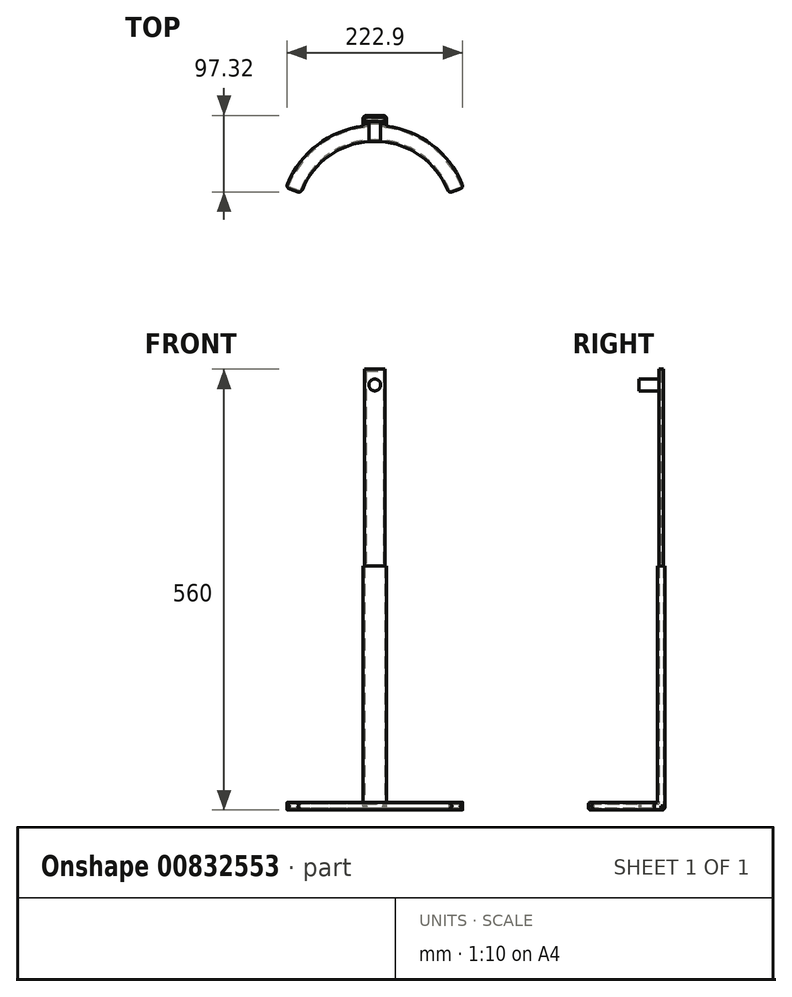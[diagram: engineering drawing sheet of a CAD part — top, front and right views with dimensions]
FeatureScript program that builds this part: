
annotation { "Feature Type Name" : "Feature", "Feature Type Description" : "" }
export const myFeature = defineFeature(function(context is Context, id is Id, definition is map)
    precondition{}
    {
        {
            var Q0;
            Q0=qCreatedBy(makeId("Right.planeOp"),FACE);
            var sketch = newSketch(context, id + "F0", { "sketchPlane" : qUnion([Q0])});
            skLineSegment(sketch, "E0.bottom", {"start": v(30, 5) * mm, "end": v(50, 5) * mm});
            skLineSegment(sketch, "E0.top", {"start": v(30, -5) * mm, "end": v(50, -5) * mm});
            skLineSegment(sketch, "E0.left", {"start": v(30, 5) * mm, "end": v(30, -5) * mm});
            skLineSegment(sketch, "E0.right", {"start": v(50, 5) * mm, "end": v(50, -5) * mm});
            skLineSegment(sketch, "E1", {"start": v(-70, 26.35) * mm, "end": v(-70, -22.57) * mm});
            skSolve(sketch);
        }
        {
            var Q0;
            Q0=makeQuery(id+"F0.imprint","IMPRINT",FACE,{"disambiguationData":[TD([[makeQuery(id+"F0.imprint","IMPRINT",EDGE,{"derivedFrom":sQuery(id+"F0.wireOp",EDGE,"E0.bottom")}),-1.0]])]});
            var Q1;
            Q1=sQuery(id+"F0.wireOp",EDGE,"E1");
            revolve(context, id + "F1", {"surfaceOperationType" : NewSurfaceOperationType.NEW, "entities" : qUnion([Q0]), "axis" : qUnion([Q1]), "revolveType" : RevolveType.SYMMETRIC, "angle" : 140 * degree});
        }
        {
            var Q0;
            Q0=qCreatedBy(makeId("Right.planeOp"),FACE);
            var sketch = newSketch(context, id + "F2", { "sketchPlane" : qUnion([Q0])});
            skLineSegment(sketch, "E2.bottom", {"start": v(41.95, 5) * mm, "end": v(62.75, 5) * mm});
            skLineSegment(sketch, "E2.top", {"start": v(41.95, -5) * mm, "end": v(62.75, -5) * mm});
            skLineSegment(sketch, "E2.left", {"start": v(41.95, 5) * mm, "end": v(41.95, -5) * mm});
            skLineSegment(sketch, "E2.right", {"start": v(62.75, 5) * mm, "end": v(62.75, -5) * mm});
            skSolve(sketch);
        }
        {
            var Q0;
            Q0=makeQuery(id+"F2.imprint","IMPRINT",FACE,{"disambiguationData":[TD([[makeQuery(id+"F2.imprint","IMPRINT",EDGE,{"derivedFrom":sQuery(id+"F2.wireOp",EDGE,"E2.bottom")}),-1.0]])]});
            extrude(context, id + "F3", {"entities" : qUnion([Q0]), "operationType" : NewBodyOperationType.ADD, "endBound" : BoundingType.SYMMETRIC, "depth" : 30 * mm, "offsetDistance" : 25 * mm});
        }
        {
            var Q0;
            Q0=makeQuery(id+"F3.boolean.opBoolean","MERGE",FACE,{"derivedFrom":[makeQuery(id+"F1.opRevolve","SWEPT_FACE",FACE,{"disambiguationData":[OSD([sQuery(id+"F0.wireOp",EDGE,"E0.bottom")])]}),makeQuery(id+"F3.opExtrude","SWEPT_FACE",FACE,{"disambiguationData":[OSD([sQuery(id+"F2.wireOp",EDGE,"E2.bottom")])]})]});
            var sketch = newSketch(context, id + "F4", { "sketchPlane" : qUnion([Q0])});
            skLineSegment(sketch, "E3.bottom", {"start": v(-15, 62.75) * mm, "end": v(15, 62.75) * mm});
            skLineSegment(sketch, "E3.top", {"start": v(-15, 52.75) * mm, "end": v(15, 52.75) * mm});
            skLineSegment(sketch, "E3.left", {"start": v(-15, 62.75) * mm, "end": v(-15, 52.75) * mm});
            skLineSegment(sketch, "E3.right", {"start": v(15, 62.75) * mm, "end": v(15, 52.75) * mm});
            skSolve(sketch);
        }
        {
            var Q0;
            Q0 = qSketchRegion(id + "F4", true);
            extrude(context, id + "F5", {"entities" : qUnion([Q0]), "operationType" : NewBodyOperationType.ADD, "depth" : 300 * mm, "offsetDistance" : 25 * mm});
        }
        {
            var Q0;
            Q0=makeQuery(id+"F5.opExtrude","CAP_FACE",FACE,{"disambiguationData":[OSD([sQuery(id+"F4.wireOp",EDGE,"E3.bottom"),sQuery(id+"F4.wireOp",EDGE,"E3.top"),sQuery(id+"F4.wireOp",EDGE,"E3.left"),sQuery(id+"F4.wireOp",EDGE,"E3.right")])],"isStart":false});
            shell(context, id + "F6", {"entities" : qUnion([Q0]), "thickness" : 2 * mm});
        }
        {
            var Q0;
            Q0=makeQuery(id+"F5.opExtrude","CAP_FACE",FACE,{"disambiguationData":[OSD([sQuery(id+"F4.wireOp",EDGE,"E3.bottom"),sQuery(id+"F4.wireOp",EDGE,"E3.top"),sQuery(id+"F4.wireOp",EDGE,"E3.left"),sQuery(id+"F4.wireOp",EDGE,"E3.right")])],"isStart":false});
            var sketch = newSketch(context, id + "F7", { "sketchPlane" : qUnion([Q0])});
            skSolve(sketch);
        }
        {
            var Q0;
            Q0 = qSketchRegion(id + "F7", true);
            var Q1;
            Q1=makeQuery(id+"F7.imprint","IMPRINT",FACE,{"disambiguationData":[TD([[makeQuery(id+"F7.imprint","IMPRINT",EDGE,{"derivedFrom":makeQuery(id+"F6.opShell","OFFSET_EDGE",EDGE,{"disambiguationData":[OSD([sQuery(id+"F4.wireOp",EDGE,"E3.bottom")])]})}),1.0]])]});
            extrude(context, id + "F8", {"entities" : qUnion([Q0, Q1]), "depth" : 250 * mm, "offsetDistance" : 25 * mm});
        }
        {
            var Q0;
            Q0=makeQuery(id+"F8.opExtrude","CAP_FACE",FACE,{"disambiguationData":[OSD([sQuery(id+"F4.wireOp",EDGE,"E3.bottom"),sQuery(id+"F4.wireOp",EDGE,"E3.top"),sQuery(id+"F4.wireOp",EDGE,"E3.left"),sQuery(id+"F4.wireOp",EDGE,"E3.right")])],"isStart":true});
            shell(context, id + "F9", {"entities" : qUnion([Q0]), "thickness" : 2 * mm});
        }
        {
            var Q0;
            Q0=makeQuery(id+"F8.opExtrude","SWEPT_FACE",FACE,{"disambiguationData":[OSD([sQuery(id+"F4.wireOp",EDGE,"E3.top")])]});
            var sketch = newSketch(context, id + "F10", { "sketchPlane" : qUnion([Q0])});
            skCircle(sketch, "E4", {"center": v(0, 535) * mm, "radius": 7.5 * mm});
            skSolve(sketch);
        }
        {
            var Q0;
            Q0=makeQuery(id+"F10.imprint","IMPRINT",FACE,{"disambiguationData":[TD([[makeQuery(id+"F10.imprint","IMPRINT",EDGE,{"derivedFrom":sQuery(id+"F10.wireOp",EDGE,"E4")}),1.0]])]});
            var Q1;
            Q1=sQuery(id+"F10.wireOp",EDGE,"E4");
            extrude(context, id + "F11", {"entities" : qUnion([Q0]), "surfaceEntities" : qUnion([Q1]), "depth" : 25 * mm, "offsetDistance" : 25 * mm});
        }
        {
            var Q0;
            Q0=makeQuery(id+"F1.opRevolve","CAP_FACE",FACE,{"disambiguationData":[OSD([sQuery(id+"F0.wireOp",EDGE,"E0.bottom"),sQuery(id+"F0.wireOp",EDGE,"E0.top"),sQuery(id+"F0.wireOp",EDGE,"E0.left"),sQuery(id+"F0.wireOp",EDGE,"E0.right")])],"isStart":false});
            var Q1;
            Q1=makeQuery(id+"F1.opRevolve","CAP_FACE",FACE,{"disambiguationData":[OSD([sQuery(id+"F0.wireOp",EDGE,"E0.bottom"),sQuery(id+"F0.wireOp",EDGE,"E0.top"),sQuery(id+"F0.wireOp",EDGE,"E0.left"),sQuery(id+"F0.wireOp",EDGE,"E0.right")])],"isStart":true});
            fillet(context, id + "F12", {"entities" : qUnion([Q0, Q1]), "radius" : 5 * mm, "tangentPropagation" : true, "rho" : 0.5, "crossSection" : FilletCrossSection.CONIC, "allowEdgeOverflow" : false});
        }
        {
            var Q0;
            Q0=makeQuery(id+"F3.opExtrude","CAP_EDGE",EDGE,{"disambiguationData":[OSD([sQuery(id+"F2.wireOp",EDGE,"E2.top")])],"isStart":false});
            var Q1;
            Q1=makeQuery(id+"F5.boolean.opBoolean","MERGE",EDGE,{"derivedFrom":[makeQuery(id+"F3.opExtrude","CAP_EDGE",EDGE,{"disambiguationData":[OSD([sQuery(id+"F2.wireOp",EDGE,"E2.right")])],"isStart":false}),makeQuery(id+"F5.opExtrude","SWEPT_EDGE",EDGE,{"disambiguationData":[OSD([sQuery(id+"F4.wireOp",EDGE,"E3.bottom"),sQuery(id+"F4.wireOp",EDGE,"E3.right")])]})]});
            var Q2;
            Q2=makeQuery(id+"F3.opExtrude","SWEPT_EDGE",EDGE,{"disambiguationData":[OSD([sQuery(id+"F2.wireOp",EDGE,"E2.top"),sQuery(id+"F2.wireOp",EDGE,"E2.right")])]});
            var Q3;
            Q3=makeQuery(id+"F5.boolean.opBoolean","MERGE",EDGE,{"derivedFrom":[makeQuery(id+"F3.opExtrude","CAP_EDGE",EDGE,{"disambiguationData":[OSD([sQuery(id+"F2.wireOp",EDGE,"E2.right")])],"isStart":true}),makeQuery(id+"F5.opExtrude","SWEPT_EDGE",EDGE,{"disambiguationData":[OSD([sQuery(id+"F4.wireOp",EDGE,"E3.bottom"),sQuery(id+"F4.wireOp",EDGE,"E3.left")])]})]});
            var Q4;
            Q4=makeQuery(id+"F3.opExtrude","CAP_EDGE",EDGE,{"disambiguationData":[OSD([sQuery(id+"F2.wireOp",EDGE,"E2.top")])],"isStart":true});
            fillet(context, id + "F13", {"entities" : qUnion([Q0, Q1, Q2, Q3, Q4]), "radius" : 5 * mm, "tangentPropagation" : true, "rho" : 0.5, "crossSection" : FilletCrossSection.CONIC, "allowEdgeOverflow" : false});
        }
    });
